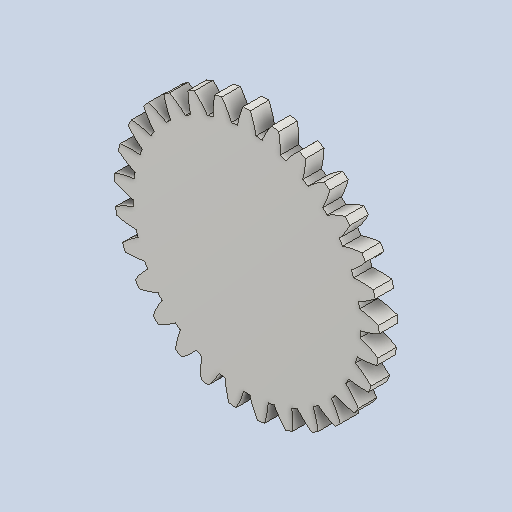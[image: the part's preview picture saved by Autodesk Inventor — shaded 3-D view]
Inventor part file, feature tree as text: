
AUTODESK INVENTOR PART (.ipt)
format: ipt  version: 2022 (Build 260153000, 153)  size: 268,288 bytes
history: native  units: mm (DEFAULTED — no unit token found)
features: plane x3, other x3, sketch x2, extrude x1
ambient origin geometry x8: Origin, YZ Plane, XZ Plane, XY Plane, X Axis, Y Axis, Z Axis, Center Point
bodies: Solid1 (feature_tree)
feature tree (9):
  extrude  "Extrusion1"  Depth=5.0mm TaperAngle=0.0deg
  plane  "Work Plane2"
  plane  "Work Plane8"
  plane  "Work Plane9"
  other  "Spur Gear"
  sketch  "Sketch1"  dims[d0=71.5mm d1=5.0mm d2=0.0mm]
  sketch  "Sketch2"  dims[d3=65.25mm d4=10.0mm d5=0.0mm d16=65.0mm d17=0.0mm d34=1.083308mm d39=0.0mm d41=0.0mm d43=65.0mm d46=65.0mm d47=0.0mm d48=0.0mm]
  other  "Srf1"
  other  "Pitch Diameter"
